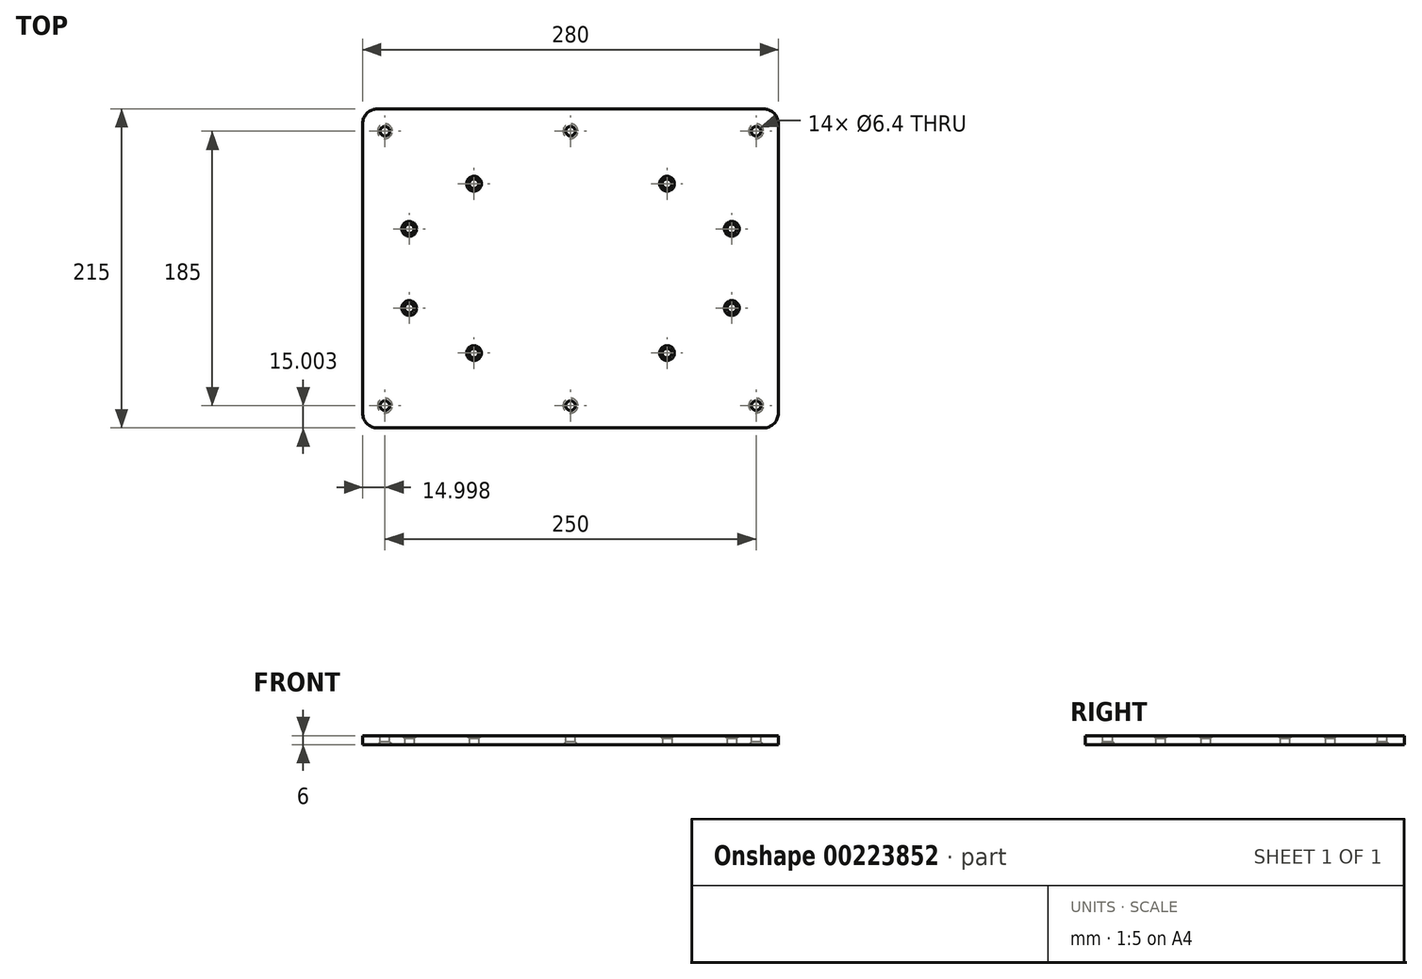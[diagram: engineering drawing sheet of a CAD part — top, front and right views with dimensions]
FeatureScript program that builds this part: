
annotation { "Feature Type Name" : "Feature", "Feature Type Description" : "" }
export const myFeature = defineFeature(function(context is Context, id is Id, definition is map)
    precondition{}
    {
        {
            var Q0;
            Q0=qCreatedBy(makeId("Top.planeOp"),FACE);
            var sketch = newSketch(context, id + "F0", { "sketchPlane" : qUnion([Q0])});
            skLineSegment(sketch, "E0.bottom", {"start": v(-220.54, 189.82) * mm, "end": v(39.46, 189.82) * mm});
            skLineSegment(sketch, "E0.top", {"start": v(-220.54, -25.18) * mm, "end": v(39.46, -25.18) * mm});
            skLineSegment(sketch, "E0.left", {"start": v(-230.54, 179.82) * mm, "end": v(-230.54, -15.18) * mm});
            skLineSegment(sketch, "E0.right", {"start": v(49.46, 179.82) * mm, "end": v(49.46, -15.18) * mm});
            skPoint(sketch, "E1.visualSharp", {"position": v(-230.54, 189.82) * mm});
            skArc(sketch, "E1.filletArc", {"start": v(-220.54, 189.82) * mm, "mid": v(-227.61, 186.9) * mm, "end": v(-230.54, 179.82) * mm});
            skPoint(sketch, "E2.visualSharp", {"position": v(49.46, 189.82) * mm});
            skArc(sketch, "E2.filletArc", {"start": v(49.46, 179.82) * mm, "mid": v(46.53, 186.9) * mm, "end": v(39.46, 189.82) * mm});
            skPoint(sketch, "E3.visualSharp", {"position": v(49.46, -25.18) * mm});
            skArc(sketch, "E3.filletArc", {"start": v(39.46, -25.18) * mm, "mid": v(46.53, -22.25) * mm, "end": v(49.46, -15.18) * mm});
            skPoint(sketch, "E4.visualSharp", {"position": v(-230.54, -25.18) * mm});
            skArc(sketch, "E4.filletArc", {"start": v(-230.54, -15.18) * mm, "mid": v(-227.61, -22.25) * mm, "end": v(-220.54, -25.18) * mm});
            skPoint(sketch, "E5.middle", {"position": v(-90.54, 82.32) * mm});
            skPoint(sketch, "E5.middle.positionSnap0", {"position": v(-90.54, -25.18) * mm});
            skPoint(sketch, "E5.middle.positionSnap1", {"position": v(49.46, 82.32) * mm});
            skPoint(sketch, "E5.centerSnap0", {"position": v(-90.54, -25.18) * mm});
            skPoint(sketch, "E5.centerSnap1", {"position": v(49.46, 82.32) * mm});
            skSolve(sketch);
        }
        {
            var Q0;
            Q0=makeQuery(id+"F0.imprint","IMPRINT",FACE,{"disambiguationData":[TD([[makeQuery(id+"F0.imprint","IMPRINT",EDGE,{"derivedFrom":sQuery(id+"F0.wireOp",EDGE,"E0.bottom")}),-1.0]])]});
            extrude(context, id + "F1", {"entities" : qUnion([Q0]), "oppositeDirection" : true, "offsetDistance" : 25 * mm, "depth" : 6 * mm});
        }
        {
            var Q0;
            Q0=makeQuery(id+"F1.opExtrude","CAP_FACE",FACE,{"disambiguationData":[OSD([sQuery(id+"F0.wireOp",EDGE,"E0.bottom"),sQuery(id+"F0.wireOp",EDGE,"E0.top"),sQuery(id+"F0.wireOp",EDGE,"E0.left"),sQuery(id+"F0.wireOp",EDGE,"E0.right"),sQuery(id+"F0.wireOp",EDGE,"E1.filletArc"),sQuery(id+"F0.wireOp",EDGE,"E2.filletArc"),sQuery(id+"F0.wireOp",EDGE,"E3.filletArc"),sQuery(id+"F0.wireOp",EDGE,"E4.filletArc")])],"isStart":false});
            var sketch = newSketch(context, id + "F2", { "sketchPlane" : qUnion([Q0])});
            skLineSegment(sketch, "E6.bottom", {"start": v(-215.54, -174.82) * mm, "end": v(34.46, -174.82) * mm});
            skLineSegment(sketch, "E6.top", {"start": v(-215.54, 10.18) * mm, "end": v(34.46, 10.18) * mm});
            skLineSegment(sketch, "E6.left", {"start": v(-215.54, -174.82) * mm, "end": v(-215.54, 10.18) * mm});
            skLineSegment(sketch, "E6.right", {"start": v(34.46, -174.82) * mm, "end": v(34.46, 10.18) * mm});
            skPoint(sketch, "E6.middle", {"position": v(-90.54, -82.32) * mm});
            skPoint(sketch, "E6.middle.positionSnap0", {"position": v(-90.54, 25.18) * mm});
            skPoint(sketch, "E6.middle.positionSnap1", {"position": v(-230.54, -82.32) * mm});
            skPoint(sketch, "E6.centerSnap0", {"position": v(-90.54, 25.18) * mm});
            skPoint(sketch, "E6.centerSnap1", {"position": v(-230.54, -82.32) * mm});
            skLineSegment(sketch, "E7", {"start": v(-90.54, 10.18) * mm, "end": v(-90.54, -174.82) * mm});
            skSolve(sketch);
        }
        {
            var Q0;
            Q0=sQuery(id+"F2.wireOp",VERTEX,"E6.left.end");
            var Q1;
            Q1=sQuery(id+"F2.wireOp",VERTEX,"E6.top.end");
            var Q2;
            Q2=sQuery(id+"F2.wireOp",VERTEX,"E6.left.start");
            var Q3;
            Q3=sQuery(id+"F2.wireOp",VERTEX,"E6.right.start");
            var Q4;
            Q4=sQuery(id+"F2.wireOp",VERTEX,"E7.start");
            var Q5;
            Q5=sQuery(id+"F2.wireOp",VERTEX,"E7.end");
            var Q6;
            Q6=makeQuery(id+"F1.opExtrude","SWEPT_BODY",BODY,{"disambiguationData":[OSD([sQuery(id+"F0.wireOp",EDGE,"E0.bottom"),sQuery(id+"F0.wireOp",EDGE,"E0.top"),sQuery(id+"F0.wireOp",EDGE,"E0.left"),sQuery(id+"F0.wireOp",EDGE,"E0.right"),sQuery(id+"F0.wireOp",EDGE,"E1.filletArc"),sQuery(id+"F0.wireOp",EDGE,"E2.filletArc"),sQuery(id+"F0.wireOp",EDGE,"E3.filletArc"),sQuery(id+"F0.wireOp",EDGE,"E4.filletArc")])]});
            hole(context, id + "F3", {"style" : HoleStyle.C_SINK, "endStyle" : HoleEndStyle.THROUGH, "holeDiameter" : 6.4 * mm, "cSinkDiameter" : 10 * mm, "cSinkAngle" : 90 * degree, "majorDiameter" : 5 * mm, "locations" : qUnion([Q0, Q1, Q2, Q3, Q4, Q5]), "scope" : qUnion([Q6]), "isTappedThrough" : true, "tappedDepth" : 12 * mm, "tapClearance" : 3, "startStyle" : HoleStartStyle.PART});
        }
        {
            var Q0;
            Q0=makeQuery(id+"F1.opExtrude","CAP_FACE",FACE,{"disambiguationData":[OSD([sQuery(id+"F0.wireOp",EDGE,"E0.bottom"),sQuery(id+"F0.wireOp",EDGE,"E0.top"),sQuery(id+"F0.wireOp",EDGE,"E0.left"),sQuery(id+"F0.wireOp",EDGE,"E0.right"),sQuery(id+"F0.wireOp",EDGE,"E1.filletArc"),sQuery(id+"F0.wireOp",EDGE,"E2.filletArc"),sQuery(id+"F0.wireOp",EDGE,"E3.filletArc"),sQuery(id+"F0.wireOp",EDGE,"E4.filletArc")])],"isStart":true});
            var sketch = newSketch(context, id + "F4", { "sketchPlane" : qUnion([Q0])});
            skEllipse(sketch, "E8", {"center": v(-90.54, 82.32) * mm, "majorRadius": 125.2 * mm, "minorRadius": 75.15 * mm, "majorAxis": v(1, 0)});
            skPoint(sketch, "E8.centerSnap0", {"position": v(-90.54, 189.82) * mm});
            skPoint(sketch, "E8.centerSnap1", {"position": v(-230.54, 82.32) * mm});
            skLineSegment(sketch, "E9.bottom", {"start": v(-199.18, 55.62) * mm, "end": v(18.1, 55.62) * mm});
            skLineSegment(sketch, "E9.top", {"start": v(-199.18, 109.02) * mm, "end": v(18.1, 109.02) * mm});
            skLineSegment(sketch, "E9.left", {"start": v(-199.18, 55.62) * mm, "end": v(-199.18, 109.02) * mm});
            skLineSegment(sketch, "E9.right", {"start": v(18.1, 55.62) * mm, "end": v(18.1, 109.02) * mm});
            skLineSegment(sketch, "E10.bottom", {"start": v(-25.54, 25.24) * mm, "end": v(-155.54, 25.24) * mm});
            skLineSegment(sketch, "E10.top", {"start": v(-25.54, 139.4) * mm, "end": v(-155.54, 139.4) * mm});
            skLineSegment(sketch, "E10.left", {"start": v(-25.54, 25.24) * mm, "end": v(-25.54, 139.4) * mm});
            skLineSegment(sketch, "E10.right", {"start": v(-155.54, 25.24) * mm, "end": v(-155.54, 139.4) * mm});
            skSolve(sketch);
        }
        {
            var Q0;
            Q0=sQuery(id+"F4.wireOp",VERTEX,"E10.top.end");
            var Q1;
            Q1=sQuery(id+"F4.wireOp",VERTEX,"E9.left.end");
            var Q2;
            Q2=sQuery(id+"F4.wireOp",VERTEX,"E9.left.start");
            var Q3;
            Q3=sQuery(id+"F4.wireOp",VERTEX,"E10.bottom.end");
            var Q4;
            Q4=sQuery(id+"F4.wireOp",VERTEX,"E10.left.start");
            var Q5;
            Q5=sQuery(id+"F4.wireOp",VERTEX,"E9.right.start");
            var Q6;
            Q6=sQuery(id+"F4.wireOp",VERTEX,"E9.right.end");
            var Q7;
            Q7=sQuery(id+"F4.wireOp",VERTEX,"E10.top.start");
            var Q8;
            Q8=makeQuery(id+"F1.opExtrude","SWEPT_BODY",BODY,{"disambiguationData":[OSD([sQuery(id+"F0.wireOp",EDGE,"E0.bottom"),sQuery(id+"F0.wireOp",EDGE,"E0.top"),sQuery(id+"F0.wireOp",EDGE,"E0.left"),sQuery(id+"F0.wireOp",EDGE,"E0.right"),sQuery(id+"F0.wireOp",EDGE,"E1.filletArc"),sQuery(id+"F0.wireOp",EDGE,"E2.filletArc"),sQuery(id+"F0.wireOp",EDGE,"E3.filletArc"),sQuery(id+"F0.wireOp",EDGE,"E4.filletArc")])]});
            hole(context, id + "F5", {"style" : HoleStyle.C_SINK, "endStyle" : HoleEndStyle.THROUGH, "holeDiameter" : 6.4 * mm, "cSinkDiameter" : 10 * mm, "cSinkAngle" : 90 * degree, "majorDiameter" : 5 * mm, "locations" : qUnion([Q0, Q1, Q2, Q3, Q4, Q5, Q6, Q7]), "scope" : qUnion([Q8]), "isTappedThrough" : true, "tappedDepth" : 12 * mm, "tapClearance" : 3, "startStyle" : HoleStartStyle.PART});
        }
    });
